# Revit family: 14-100-010_Green_simplified
name_source: partatom
category: Generic Models
units: mm (PartAtom-declared; Revit-internal decimal feet)

## family parameters
Always vertical = Yes
Can host rebar = No
Cut with Voids When Loaded = No
Part Type = Normal
Room Calculation Point = No
Round Connector Dimension = Use Diameter
Shared = No
Work Plane-Based = No

## types (1)
- Type 1
    Artnr_Green_simplified = 14-100-010
    CheckedDate = -
    CheckedDate_Green_simplified = -
    Default Elevation = 0 mm  [stored 0 ft]
    Description = Haukeli
    Number = 20067
    Number_Green_simplified = 20067
    PartName = Haukeli
    PartName_Green_simplified = Haukeli
    Revision = 0
    Revision_Green_simplified = 0
    UNIT_OF_MEASURE_Green_simplified = - none -
    Weight_Green_simplified = 36943596.40

note: [stored X ft] marks values corroborated as IEEE doubles in the binary element streams (Revit-internal decimal feet)

## geometry (parser evidence)
native form markers: Sweep x37
no freeform markers — native parametric forms only
